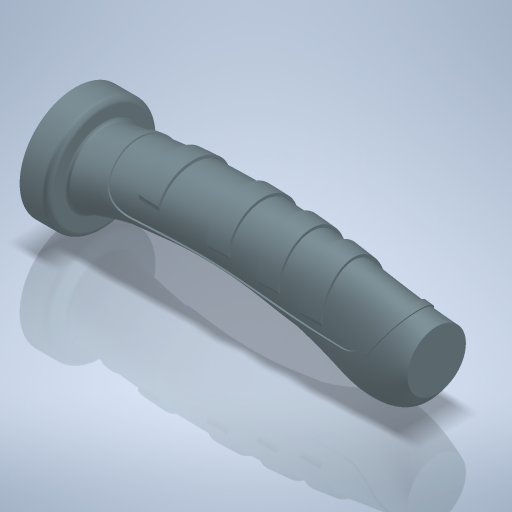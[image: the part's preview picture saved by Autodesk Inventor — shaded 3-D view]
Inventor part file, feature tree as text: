
AUTODESK INVENTOR PART (.ipt)
format: ipt  version: 2024 (Build 280153000, 153)  size: 3,418,624 bytes
history: native  units: mm
features: other x15, sketch x6, plane x4, fillet x3, loft x1, shell x1, extrude x1, projected_geometry x1
ambient origin geometry x8: Origin, YZ Plane, XZ Plane, XY Plane, X Axis, Y Axis, Z Axis, Center Point
bodies: Body1 (feature_tree)
feature tree (32):
  sketch  "Skizze6"  dims[d35=240.0mm d36=550.0mm d37=210.0mm]
  plane  "Arbeitsebene3"
  sketch  "Skizze7"  dims[d38=40.0mm d39=42.0mm d40=52.0mm d41=0.0mm d42=52.0mm]
  plane  "Arbeitsebene4"
  loft  "Erhebung1"
  shell  "Wandung1"  Thickness=210.0mm
  extrude  "Extrusion4"  Depth=42.0mm
  fillet  "Rundung2"  Radius=52.0mm
  fillet  "Rundung3"  [1 undecoded]
  plane  "Arbeitsebene7"
  sketch  "Skizze10"  dims[d44=42.0mm]
  other  "3D-Skizze4"
  other  "Trennen1"
  other  "Trennen2"
  other  "Trennen3"
  other  "Trennen4"
  other  "Verdickung1"
  other  "Verdickung2"
  other  "Verdickung3"
  other  "Verdickung4"
  plane  "Arbeitsebene8"
  sketch  "Skizze15"  dims[d47=0.0mm d48=90.0deg d49=0.0mm d50=90.0deg d51=0.0mm d52=90.0deg d53=2.0mm d57=26.0mm d59=2.0mm d60=15.0mm d61=15.0mm d62=15.0mm d63=15.0mm d64=60.0mm d65=90.0mm d66=125.0mm d69=80.0mm d70=20.0mm d71=0.0mm d72=4.0mm d73=2.0mm d74=20.0mm d75=5.0mm d76=5.0mm d77=5.0mm d78=70.0mm d79=2.0mm d80=2.0mm d81=2.0mm d82=2.0mm d83=2.0mm d84=2.0mm d85=2.0mm d86=2.0mm d87=2.0mm d88=2.0mm d89=2.0mm d90=2.0mm d91=26.0mm d92=2.0mm d96=2.0mm d97=5.0mm d99=20.0mm d100=12.0mm d102=2.0mm d103=2.0mm d107=45.0mm d110=12.0mm d120=22.0mm d121=20.0mm d124=150.0mm d125=65.0mm d126=1.0mm d127=1.0mm d128=5.0mm d14=0.5mm d15=0.872665mm d16=0.5mm d17=0.872665mm]
  other  "3D-Skizze6"
  other  "Trennen5"
  other  "Trennen6"
  other  "Verdickung5"
  fillet  "Rundung4"  Radius=52.0mm
  sketch  "Skizze8"  dims[d43=240.0mm]
  projected_geometry  "Projizierte Kontur2"
  sketch  "Skizze11"  dims[d45=0.0mm d46=90.0deg]
  other  "Projekt aus Skizze10"
  other  "Auf Fläche projizieren2"
note: 1 required parameter value undecoded (feature->parameter linkage not recoverable at this tier; creation-order binding heuristic only, values carry confidence <= 0.55)
